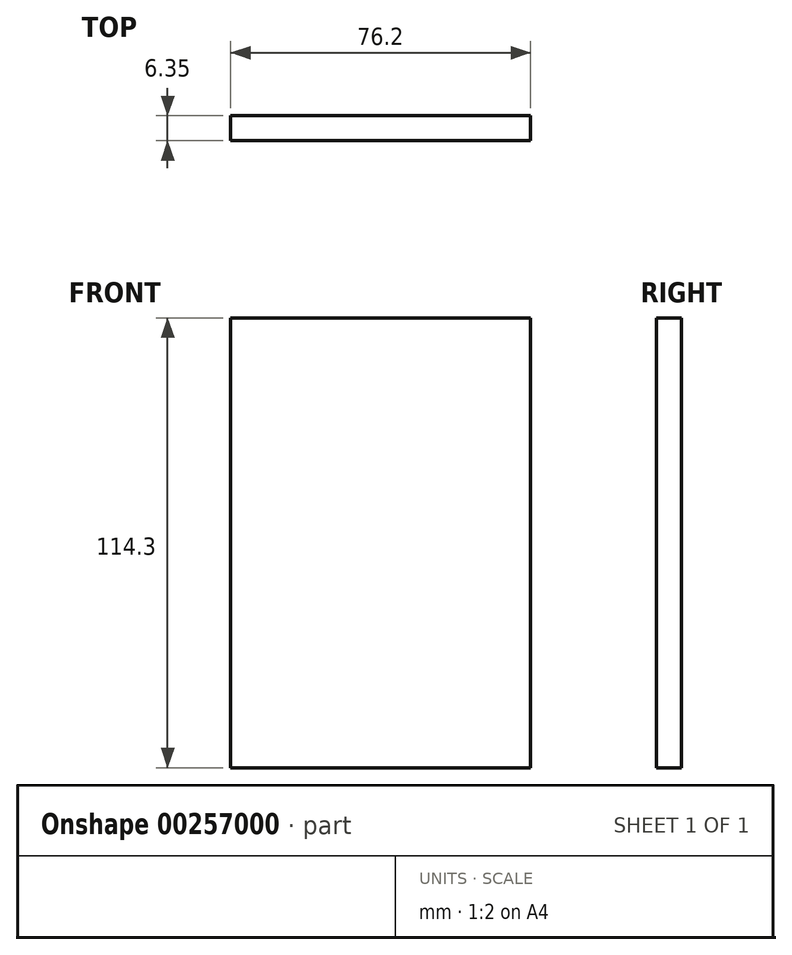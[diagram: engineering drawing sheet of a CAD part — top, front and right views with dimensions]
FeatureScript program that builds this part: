
annotation { "Feature Type Name" : "Feature", "Feature Type Description" : "" }
export const myFeature = defineFeature(function(context is Context, id is Id, definition is map)
    precondition{}
    {
        {
            var Q0;
            Q0=qCreatedBy(makeId("Front.planeOp"),FACE);
            var sketch = newSketch(context, id + "F0", { "sketchPlane" : qUnion([Q0])});
            skLineSegment(sketch, "E0.bottom", {"start": v(-51.27, 34.48) * mm, "end": v(24.93, 34.48) * mm});
            skLineSegment(sketch, "E0.top", {"start": v(-51.27, -79.82) * mm, "end": v(24.93, -79.82) * mm});
            skLineSegment(sketch, "E0.left", {"start": v(-51.27, 34.48) * mm, "end": v(-51.27, -79.82) * mm});
            skLineSegment(sketch, "E0.right", {"start": v(24.93, 34.48) * mm, "end": v(24.93, -79.82) * mm});
            skSolve(sketch);
        }
        {
            var Q0;
            Q0 = qSketchRegion(id + "F0", true);
            extrude(context, id + "F1", {"entities" : qUnion([Q0]), "depth" : 6.35 * mm});
        }
    });
